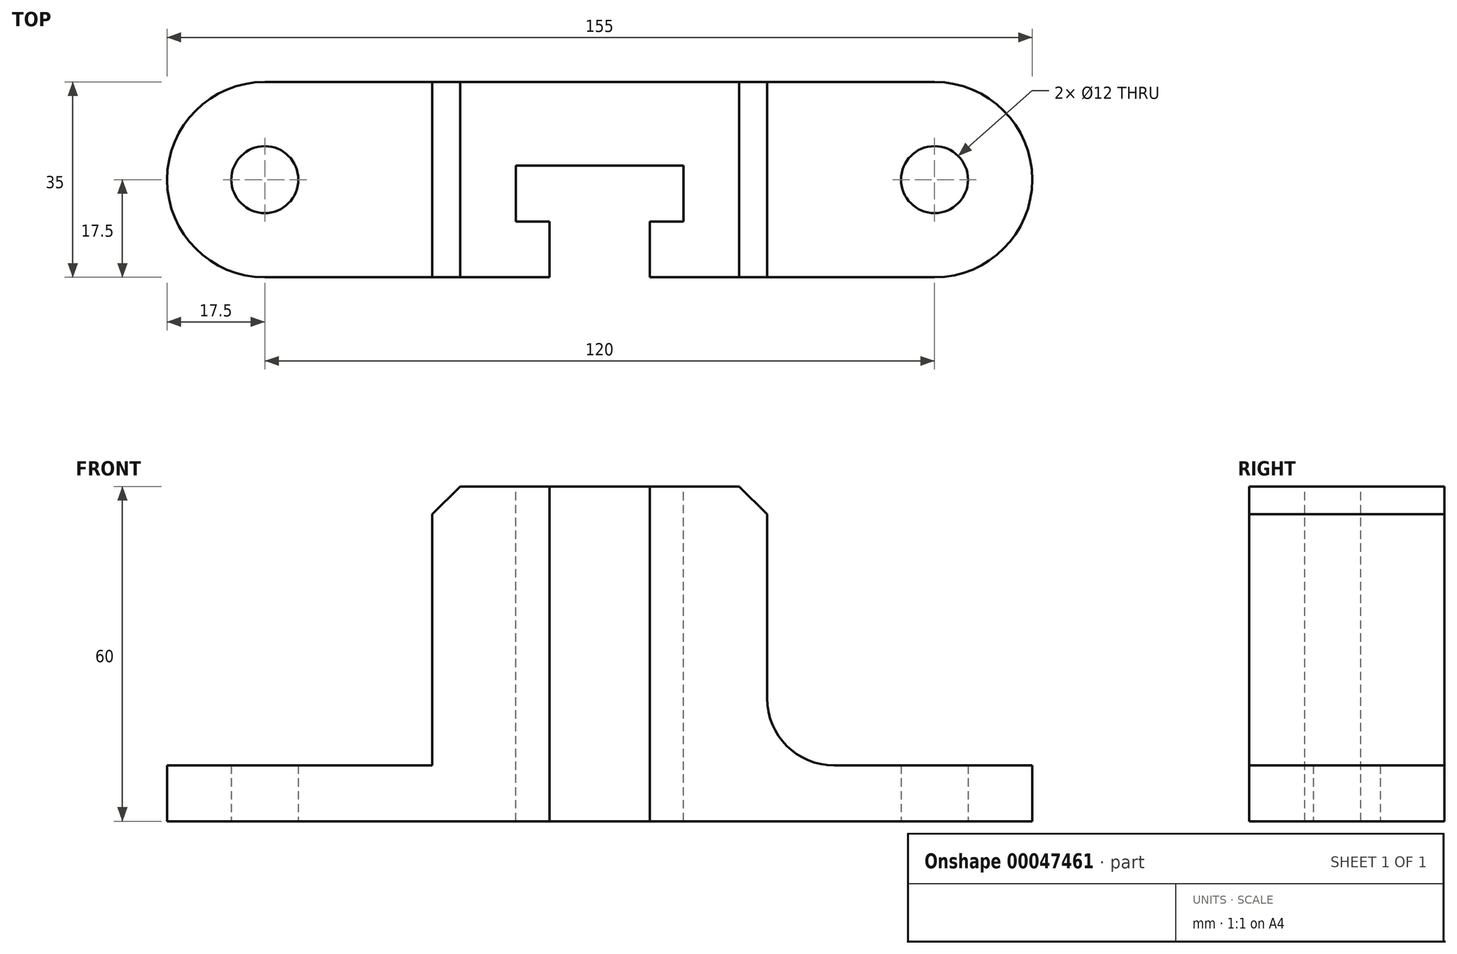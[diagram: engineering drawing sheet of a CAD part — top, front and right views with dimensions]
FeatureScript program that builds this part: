
annotation { "Feature Type Name" : "Feature", "Feature Type Description" : "" }
export const myFeature = defineFeature(function(context is Context, id is Id, definition is map)
    precondition{}
    {
        {
            var Q0;
            Q0=qCreatedBy(makeId("Top.planeOp"),FACE);
            var sketch = newSketch(context, id + "F0", { "sketchPlane" : qUnion([Q0])});
            skLineSegment(sketch, "E0", {"start": v(-60, 0) * mm, "end": v(60, 0) * mm, "construction": true});
            skCircle(sketch, "E1", {"center": v(-60, 0) * mm, "radius": 6 * mm});
            skCircle(sketch, "E2", {"center": v(60, 0) * mm, "radius": 6 * mm});
            skArc(sketch, "E3", {"start": v(-60, 17.5) * mm, "mid": v(-77.5, 0) * mm, "end": v(-60, -17.5) * mm});
            skArc(sketch, "E4", {"start": v(60, -17.5) * mm, "mid": v(77.5, 0) * mm, "end": v(60, 17.5) * mm});
            skLineSegment(sketch, "E5", {"start": v(-60, 0) * mm, "end": v(-60, 17.5) * mm, "construction": true});
            skLineSegment(sketch, "E6", {"start": v(-60, 0) * mm, "end": v(-60, -17.5) * mm, "construction": true});
            skLineSegment(sketch, "E7", {"start": v(60, 0) * mm, "end": v(60, 17.5) * mm, "construction": true});
            skLineSegment(sketch, "E8", {"start": v(60, 0) * mm, "end": v(60, -17.5) * mm, "construction": true});
            skLineSegment(sketch, "E9", {"start": v(-60, 17.5) * mm, "end": v(60, 17.5) * mm});
            skLineSegment(sketch, "E10", {"start": v(-60, -17.5) * mm, "end": v(60, -17.5) * mm});
            skSolve(sketch);
        }
        {
            var Q0;
            Q0 = qSketchRegion(id + "F0", true);
            extrude(context, id + "F1", {"entities" : qUnion([Q0]), "depth" : 10 * mm});
        }
        {
            var Q0;
            Q0=makeQuery(id+"F1.opExtrude","CAP_FACE",FACE,{"disambiguationData":[OSD([sQuery(id+"F0.wireOp",EDGE,"E1"),sQuery(id+"F0.wireOp",EDGE,"E2"),sQuery(id+"F0.wireOp",EDGE,"E3"),sQuery(id+"F0.wireOp",EDGE,"E4"),sQuery(id+"F0.wireOp",EDGE,"E9"),sQuery(id+"F0.wireOp",EDGE,"E10")])],"isStart":false});
            var sketch = newSketch(context, id + "F2", { "sketchPlane" : qUnion([Q0])});
            skLineSegment(sketch, "E11.rect.bottom", {"start": v(30, 17.5) * mm, "end": v(-30, 17.5) * mm});
            skLineSegment(sketch, "E11.rect.top", {"start": v(30, -17.5) * mm, "end": v(-30, -17.5) * mm});
            skLineSegment(sketch, "E11.rect.left", {"start": v(30, 17.5) * mm, "end": v(30, -17.5) * mm});
            skLineSegment(sketch, "E11.rect.right", {"start": v(-30, 17.5) * mm, "end": v(-30, -17.5) * mm});
            skPoint(sketch, "E11.rect.middle", {"position": v(0, 0) * mm});
            skSolve(sketch);
        }
        {
            var Q0;
            Q0 = qSketchRegion(id + "F2", true);
            extrude(context, id + "F3", {"entities" : qUnion([Q0]), "operationType" : NewBodyOperationType.ADD, "depth" : 50 * mm});
        }
        {
            var Q0;
            Q0=makeQuery(id+"F3.opExtrude","CAP_EDGE",EDGE,{"disambiguationData":[OSD([sQuery(id+"F2.wireOp",EDGE,"E11.rect.left")])],"isStart":true});
            var Q1;
            Q1=makeQuery(id+"F3.opExtrude","CAP_EDGE",EDGE,{"disambiguationData":[OSD([sQuery(id+"F2.wireOp",EDGE,"E11.rect.right")])],"isStart":true});
            fillet(context, id + "F4", {"entities" : qUnion([Q0, Q1]), "radius" : 12 * mm, "tangentPropagation" : true, "allowEdgeOverflow" : false});
        }
        {
            var Q0;
            Q0=makeQuery(id+"F3.opExtrude","CAP_EDGE",EDGE,{"disambiguationData":[OSD([sQuery(id+"F2.wireOp",EDGE,"E11.rect.left")])],"isStart":false});
            var Q1;
            Q1=makeQuery(id+"F3.opExtrude","CAP_EDGE",EDGE,{"disambiguationData":[OSD([sQuery(id+"F2.wireOp",EDGE,"E11.rect.right")])],"isStart":false});
            chamfer(context, id + "F5", {"entities" : qUnion([Q0, Q1]), "chamferType" : ChamferType.OFFSET_ANGLE, "width" : 5 * mm, "oppositeDirection" : false, "angle" : 45 * degree, "tangentPropagation" : true});
        }
        {
            var Q0;
            Q0=makeQuery(id+"F3.opExtrude","CAP_FACE",FACE,{"disambiguationData":[OSD([sQuery(id+"F2.wireOp",EDGE,"E11.rect.bottom"),sQuery(id+"F2.wireOp",EDGE,"E11.rect.top"),sQuery(id+"F2.wireOp",EDGE,"E11.rect.left"),sQuery(id+"F2.wireOp",EDGE,"E11.rect.right")])],"isStart":false});
            var sketch = newSketch(context, id + "F6", { "sketchPlane" : qUnion([Q0])});
            skLineSegment(sketch, "E12", {"start": v(-9, -17.5) * mm, "end": v(9, -17.5) * mm});
            skLineSegment(sketch, "E13", {"start": v(9, -17.5) * mm, "end": v(9, -7.5) * mm});
            skLineSegment(sketch, "E14", {"start": v(9, -7.5) * mm, "end": v(15, -7.5) * mm});
            skLineSegment(sketch, "E15", {"start": v(15, -7.5) * mm, "end": v(15, 2.5) * mm});
            skLineSegment(sketch, "E16", {"start": v(15, 2.5) * mm, "end": v(-15, 2.5) * mm});
            skLineSegment(sketch, "E17", {"start": v(-15, 2.5) * mm, "end": v(-15, -7.5) * mm});
            skLineSegment(sketch, "E18", {"start": v(-15, -7.5) * mm, "end": v(-9, -7.5) * mm});
            skLineSegment(sketch, "E19", {"start": v(-9, -7.5) * mm, "end": v(-9, -17.5) * mm});
            skSolve(sketch);
        }
        {
            var Q0;
            Q0 = qSketchRegion(id + "F6", true);
            extrude(context, id + "F7", {"entities" : qUnion([Q0]), "operationType" : NewBodyOperationType.REMOVE, "endBound" : BoundingType.THROUGH_ALL, "oppositeDirection" : true, "depth" : 25 * mm});
        }
    });
